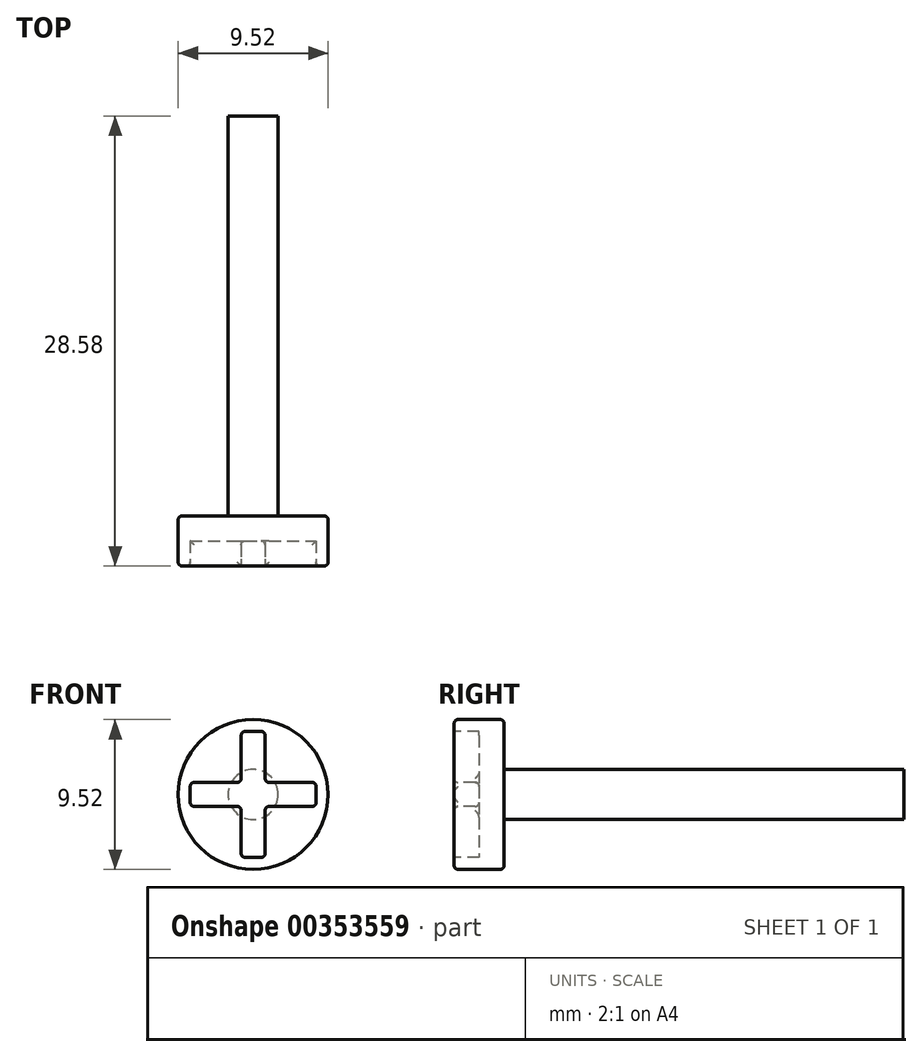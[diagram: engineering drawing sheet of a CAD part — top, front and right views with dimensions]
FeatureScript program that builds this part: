
annotation { "Feature Type Name" : "Feature", "Feature Type Description" : "" }
export const myFeature = defineFeature(function(context is Context, id is Id, definition is map)
    precondition{}
    {
        {
            var Q0;
            Q0=qCreatedBy(makeId("Front.planeOp"),FACE);
            var sketch = newSketch(context, id + "F0", { "sketchPlane" : qUnion([Q0])});
            skCircle(sketch, "E0", {"center": v(0, 0) * mm, "radius": 1.59 * mm});
            skSolve(sketch);
        }
        {
            var Q0;
            Q0 = qSketchRegion(id + "F0", true);
            extrude(context, id + "F1", {"entities" : qUnion([Q0]), "depth" : 25.4 * mm, "symmetric" : true});
        }
        {
            var Q0;
            Q0=makeQuery(id+"F1.opExtrude","CAP_FACE",FACE,{"disambiguationData":[OSD([sQuery(id+"F0.wireOp",EDGE,"E0")])],"isStart":false});
            var sketch = newSketch(context, id + "F2", { "sketchPlane" : qUnion([Q0])});
            skCircle(sketch, "E1", {"center": v(0, 0) * mm, "radius": 4.76 * mm});
            skSolve(sketch);
        }
        {
            var Q0;
            Q0 = qSketchRegion(id + "F2", true);
            extrude(context, id + "F3", {"entities" : qUnion([Q0]), "operationType" : NewBodyOperationType.ADD, "depth" : 3.17 * mm});
        }
        {
            var Q0;
            Q0=makeQuery(id+"F3.opExtrude","CAP_FACE",FACE,{"disambiguationData":[OSD([sQuery(id+"F2.wireOp",EDGE,"E1")])],"isStart":false});
            var sketch = newSketch(context, id + "F4", { "sketchPlane" : qUnion([Q0])});
            skLineSegment(sketch, "E2.bottom", {"start": v(-0.76, 4) * mm, "end": v(0.76, 4) * mm});
            skLineSegment(sketch, "E2.top", {"start": v(-0.76, -4) * mm, "end": v(0.76, -4) * mm});
            skLineSegment(sketch, "E2.left", {"start": v(-0.76, 4) * mm, "end": v(-0.76, -4) * mm});
            skLineSegment(sketch, "E2.right", {"start": v(0.76, 4) * mm, "end": v(0.76, -4) * mm});
            skLineSegment(sketch, "E3.bottom", {"start": v(-4, 0.76) * mm, "end": v(4, 0.76) * mm});
            skLineSegment(sketch, "E3.top", {"start": v(-4, -0.76) * mm, "end": v(4, -0.76) * mm});
            skLineSegment(sketch, "E3.left", {"start": v(-4, 0.76) * mm, "end": v(-4, -0.76) * mm});
            skLineSegment(sketch, "E3.right", {"start": v(4, 0.76) * mm, "end": v(4, -0.76) * mm});
            skSolve(sketch);
        }
        {
            var Q0;
            Q0 = qSketchRegion(id + "F4", true);
            extrude(context, id + "F5", {"entities" : qUnion([Q0]), "operationType" : NewBodyOperationType.REMOVE, "oppositeDirection" : true, "depth" : 1.59 * mm});
        }
        {
            var Q0;
            Q0=makeQuery(id+"F3.opExtrude","CAP_EDGE",EDGE,{"disambiguationData":[OSD([sQuery(id+"F2.wireOp",EDGE,"E1")])],"isStart":false});
            var Q1;
            {var subQ0=sQuery(id+"F4.wireOp",EDGE,"E3.bottom");Q1=makeQuery(id+"F5.boolean.opBoolean","COPY",EDGE,{"derivedFrom":makeQuery(id+"F5.opExtrude","CAP_EDGE",EDGE,{"disambiguationData":[OSD([subQ0]),TDD([makeQuery(id+"F4.imprint","IMPRINT",EDGE,{"disambiguationData":[TD([[makeQuery(id+"F4.imprint","INTERSECT",VERTEX,{"derivedFrom":[subQ0,sQuery(id+"F4.wireOp",EDGE,"E3.left")]}),-1.0]])],"derivedFrom":subQ0})])],"isStart":true})});}
            var Q2;
            {var subQ0=sQuery(id+"F4.wireOp",EDGE,"E2.left");Q2=makeQuery(id+"F5.boolean.opBoolean","COPY",EDGE,{"derivedFrom":makeQuery(id+"F5.opExtrude","CAP_EDGE",EDGE,{"disambiguationData":[OSD([subQ0]),TDD([makeQuery(id+"F4.imprint","IMPRINT",EDGE,{"disambiguationData":[TD([[makeQuery(id+"F4.imprint","INTERSECT",VERTEX,{"derivedFrom":[sQuery(id+"F4.wireOp",EDGE,"E2.bottom"),subQ0]}),-1.0]])],"derivedFrom":subQ0})])],"isStart":true})});}
            var Q3;
            {var subQ0=sQuery(id+"F4.wireOp",EDGE,"E2.right");Q3=makeQuery(id+"F5.boolean.opBoolean","COPY",EDGE,{"derivedFrom":makeQuery(id+"F5.opExtrude","CAP_EDGE",EDGE,{"disambiguationData":[OSD([subQ0]),TDD([makeQuery(id+"F4.imprint","IMPRINT",EDGE,{"disambiguationData":[TD([[makeQuery(id+"F4.imprint","INTERSECT",VERTEX,{"derivedFrom":[sQuery(id+"F4.wireOp",EDGE,"E2.bottom"),subQ0]}),-1.0]])],"derivedFrom":subQ0})])],"isStart":true})});}
            var Q4;
            {var subQ0=sQuery(id+"F4.wireOp",EDGE,"E3.top");Q4=makeQuery(id+"F5.boolean.opBoolean","COPY",EDGE,{"derivedFrom":makeQuery(id+"F5.opExtrude","CAP_EDGE",EDGE,{"disambiguationData":[OSD([subQ0]),TDD([makeQuery(id+"F4.imprint","IMPRINT",EDGE,{"disambiguationData":[TD([[makeQuery(id+"F4.imprint","INTERSECT",VERTEX,{"derivedFrom":[subQ0,sQuery(id+"F4.wireOp",EDGE,"E3.left")]}),-1.0]])],"derivedFrom":subQ0})])],"isStart":true})});}
            var Q5;
            {var subQ0=sQuery(id+"F4.wireOp",EDGE,"E2.left");Q5=makeQuery(id+"F5.boolean.opBoolean","COPY",EDGE,{"derivedFrom":makeQuery(id+"F5.opExtrude","CAP_EDGE",EDGE,{"disambiguationData":[OSD([subQ0]),TDD([makeQuery(id+"F4.imprint","IMPRINT",EDGE,{"disambiguationData":[TD([[makeQuery(id+"F4.imprint","INTERSECT",VERTEX,{"derivedFrom":[sQuery(id+"F4.wireOp",EDGE,"E2.top"),subQ0]}),1.0]])],"derivedFrom":subQ0})])],"isStart":true})});}
            var Q6;
            {var subQ0=sQuery(id+"F4.wireOp",EDGE,"E3.top");Q6=makeQuery(id+"F5.boolean.opBoolean","COPY",EDGE,{"derivedFrom":makeQuery(id+"F5.opExtrude","CAP_EDGE",EDGE,{"disambiguationData":[OSD([subQ0]),TDD([makeQuery(id+"F4.imprint","IMPRINT",EDGE,{"disambiguationData":[TD([[makeQuery(id+"F4.imprint","INTERSECT",VERTEX,{"derivedFrom":[subQ0,sQuery(id+"F4.wireOp",EDGE,"E3.right")]}),1.0]])],"derivedFrom":subQ0})])],"isStart":true})});}
            var Q7;
            {var subQ0=sQuery(id+"F4.wireOp",EDGE,"E3.bottom");Q7=makeQuery(id+"F5.boolean.opBoolean","COPY",EDGE,{"derivedFrom":makeQuery(id+"F5.opExtrude","CAP_EDGE",EDGE,{"disambiguationData":[OSD([subQ0]),TDD([makeQuery(id+"F4.imprint","IMPRINT",EDGE,{"disambiguationData":[TD([[makeQuery(id+"F4.imprint","INTERSECT",VERTEX,{"derivedFrom":[subQ0,sQuery(id+"F4.wireOp",EDGE,"E3.right")]}),1.0]])],"derivedFrom":subQ0})])],"isStart":true})});}
            var Q8;
            {var subQ0=sQuery(id+"F4.wireOp",EDGE,"E3.bottom");Q8=makeQuery(id+"F5.boolean.opBoolean","COPY",FACE,{"derivedFrom":makeQuery(id+"F5.opExtrude","SWEPT_FACE",FACE,{"disambiguationData":[OSD([subQ0]),TDD([makeQuery(id+"F4.imprint","IMPRINT",EDGE,{"disambiguationData":[TD([[makeQuery(id+"F4.imprint","INTERSECT",VERTEX,{"derivedFrom":[subQ0,sQuery(id+"F4.wireOp",EDGE,"E3.left")]}),-1.0]])],"derivedFrom":subQ0})])]})});}
            var Q9;
            {var subQ0=sQuery(id+"F4.wireOp",EDGE,"E3.bottom");Q9=makeQuery(id+"F5.boolean.opBoolean","COPY",FACE,{"derivedFrom":makeQuery(id+"F5.opExtrude","SWEPT_FACE",FACE,{"disambiguationData":[OSD([subQ0]),TDD([makeQuery(id+"F4.imprint","IMPRINT",EDGE,{"disambiguationData":[TD([[makeQuery(id+"F4.imprint","INTERSECT",VERTEX,{"derivedFrom":[subQ0,sQuery(id+"F4.wireOp",EDGE,"E3.right")]}),1.0]])],"derivedFrom":subQ0})])]})});}
            var Q10;
            {var subQ0=sQuery(id+"F4.wireOp",EDGE,"E3.top");Q10=makeQuery(id+"F5.boolean.opBoolean","COPY",FACE,{"derivedFrom":makeQuery(id+"F5.opExtrude","SWEPT_FACE",FACE,{"disambiguationData":[OSD([subQ0]),TDD([makeQuery(id+"F4.imprint","IMPRINT",EDGE,{"disambiguationData":[TD([[makeQuery(id+"F4.imprint","INTERSECT",VERTEX,{"derivedFrom":[subQ0,sQuery(id+"F4.wireOp",EDGE,"E3.left")]}),-1.0]])],"derivedFrom":subQ0})])]})});}
            var Q11;
            {var subQ0=sQuery(id+"F4.wireOp",EDGE,"E3.top");Q11=makeQuery(id+"F5.boolean.opBoolean","COPY",FACE,{"derivedFrom":makeQuery(id+"F5.opExtrude","SWEPT_FACE",FACE,{"disambiguationData":[OSD([subQ0]),TDD([makeQuery(id+"F4.imprint","IMPRINT",EDGE,{"disambiguationData":[TD([[makeQuery(id+"F4.imprint","INTERSECT",VERTEX,{"derivedFrom":[subQ0,sQuery(id+"F4.wireOp",EDGE,"E3.right")]}),1.0]])],"derivedFrom":subQ0})])]})});}
            var Q12;
            Q12=makeQuery(id+"F5.boolean.opBoolean","COPY",EDGE,{"derivedFrom":makeQuery(id+"F5.opExtrude","CAP_EDGE",EDGE,{"disambiguationData":[OSD([sQuery(id+"F4.wireOp",EDGE,"E2.bottom")])],"isStart":true})});
            var Q13;
            Q13=makeQuery(id+"F5.boolean.opBoolean","COPY",EDGE,{"derivedFrom":makeQuery(id+"F5.opExtrude","CAP_EDGE",EDGE,{"disambiguationData":[OSD([sQuery(id+"F4.wireOp",EDGE,"E2.top")])],"isStart":true})});
            var Q14;
            Q14=makeQuery(id+"F5.boolean.opBoolean","COPY",EDGE,{"derivedFrom":makeQuery(id+"F5.opExtrude","SWEPT_EDGE",EDGE,{"disambiguationData":[OSD([sQuery(id+"F4.wireOp",EDGE,"E2.bottom"),sQuery(id+"F4.wireOp",EDGE,"E2.right")])]})});
            var Q15;
            Q15=makeQuery(id+"F5.boolean.opBoolean","COPY",EDGE,{"derivedFrom":makeQuery(id+"F5.opExtrude","SWEPT_EDGE",EDGE,{"disambiguationData":[OSD([sQuery(id+"F4.wireOp",EDGE,"E2.bottom"),sQuery(id+"F4.wireOp",EDGE,"E2.left")])]})});
            var Q16;
            Q16=makeQuery(id+"F5.boolean.opBoolean","COPY",EDGE,{"derivedFrom":makeQuery(id+"F5.opExtrude","SWEPT_EDGE",EDGE,{"disambiguationData":[OSD([sQuery(id+"F4.wireOp",EDGE,"E2.top"),sQuery(id+"F4.wireOp",EDGE,"E2.right")])]})});
            var Q17;
            Q17=makeQuery(id+"F5.boolean.opBoolean","COPY",EDGE,{"derivedFrom":makeQuery(id+"F5.opExtrude","SWEPT_EDGE",EDGE,{"disambiguationData":[OSD([sQuery(id+"F4.wireOp",EDGE,"E2.top"),sQuery(id+"F4.wireOp",EDGE,"E2.left")])]})});
            var Q18;
            Q18=makeQuery(id+"F3.opExtrude","CAP_EDGE",EDGE,{"disambiguationData":[OSD([sQuery(id+"F2.wireOp",EDGE,"E1")])],"isStart":true});
            fillet(context, id + "F6", {"entities" : qUnion([Q0, Q1, Q2, Q3, Q4, Q5, Q6, Q7, Q8, Q9, Q10, Q11, Q12, Q13, Q14, Q15, Q16, Q17, Q18]), "radius" : 0.25 * mm, "tangentPropagation" : true, "allowEdgeOverflow" : false});
        }
    });
